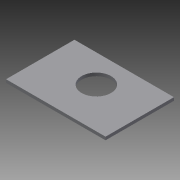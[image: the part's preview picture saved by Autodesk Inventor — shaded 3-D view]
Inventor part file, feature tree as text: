
AUTODESK INVENTOR PART (.ipt)
format: ipt  version: 2013 (Build 170138000, 138)  size: 81,920 bytes
history: native  units: in
note: dims shown in document units (in); Inventor stores cm internally (conversion verified against a paired STEP export)
features: extrude x2, sketch x2
ambient origin geometry x8: Origin, YZ Plane, XZ Plane, XY Plane, X Axis, Y Axis, Z Axis, Center Point
bodies: Solid1 (feature_tree)
feature tree (4):
  extrude  "Extrusion1"  Depth=4.0in
  extrude  "Extrusion2"  Depth=1.1811in
  sketch  "Sketch1"  dims[d4=0.125in d5=0.0in d6=4.0in]
  sketch  "Sketch2"  dims[d7=2.75in d8=1.1811in d9=2.0in d10=2.0in d11=1.63in d12=1.375in d13=0.125in d14=0.0in]
